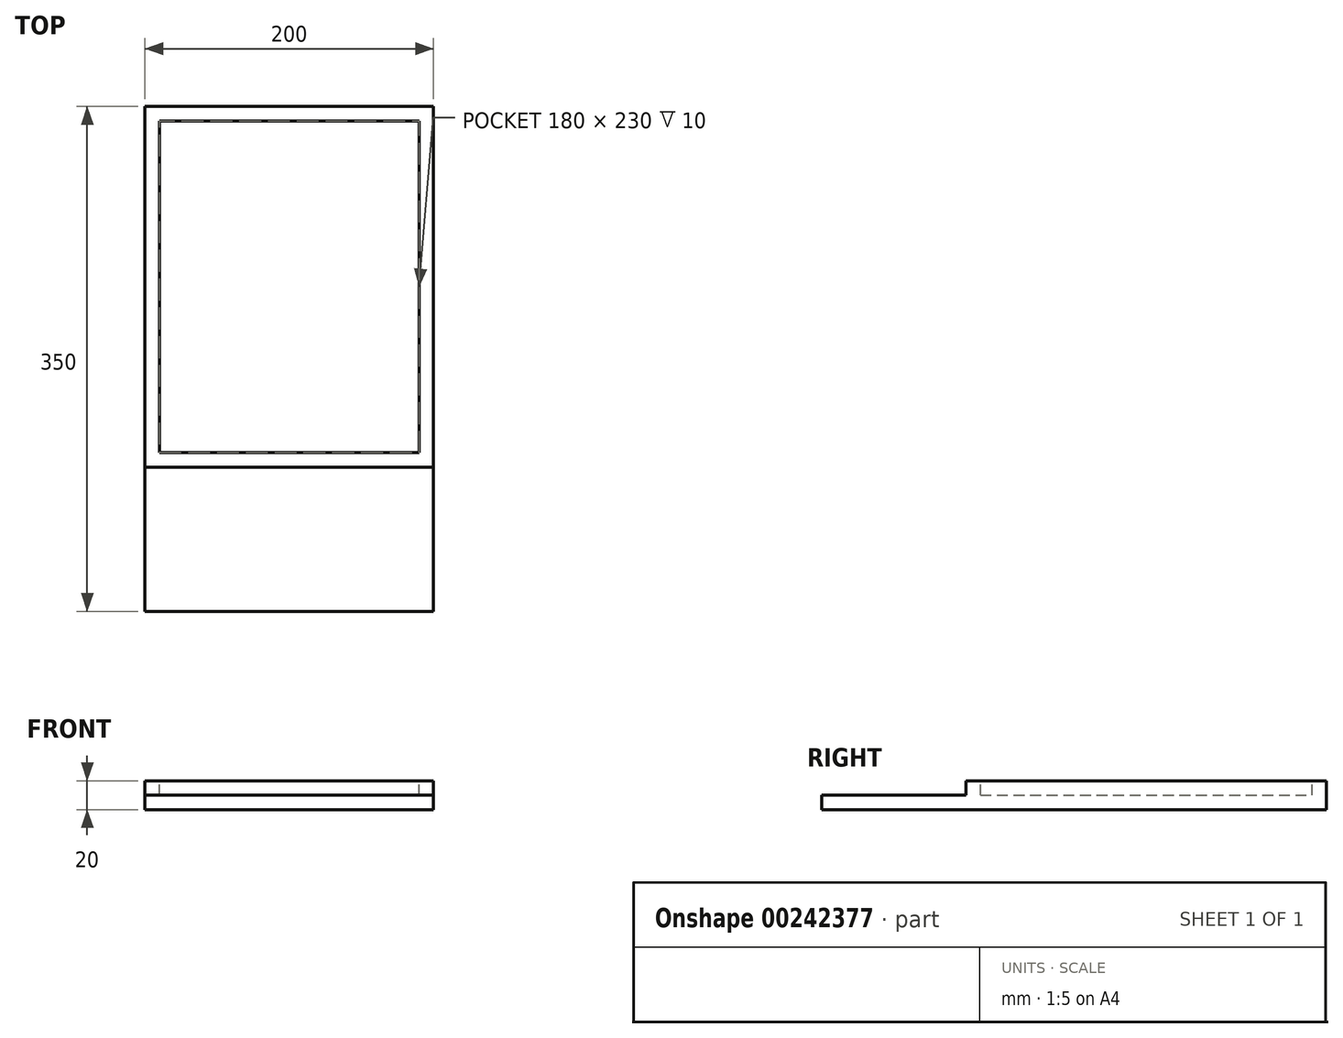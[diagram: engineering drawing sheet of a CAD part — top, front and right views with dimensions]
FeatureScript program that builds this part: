
annotation { "Feature Type Name" : "Feature", "Feature Type Description" : "" }
export const myFeature = defineFeature(function(context is Context, id is Id, definition is map)
    precondition{}
    {
        {
            var Q0;
            Q0=qCreatedBy(makeId("Top.planeOp"),FACE);
            var sketch = newSketch(context, id + "F0", { "sketchPlane" : qUnion([Q0])});
            skLineSegment(sketch, "E0.bottom", {"start": v(-59, -123.05) * mm, "end": v(141, -123.05) * mm});
            skLineSegment(sketch, "E0.top", {"start": v(-59, 126.95) * mm, "end": v(141, 126.95) * mm});
            skLineSegment(sketch, "E0.left", {"start": v(-59, -123.05) * mm, "end": v(-59, 126.95) * mm});
            skLineSegment(sketch, "E0.right", {"start": v(141, -123.05) * mm, "end": v(141, 126.95) * mm});
            skLineSegment(sketch, "E1.top", {"start": v(-59, -223.05) * mm, "end": v(141, -223.05) * mm});
            skLineSegment(sketch, "E1.left", {"start": v(-59, -123.05) * mm, "end": v(-59, -223.05) * mm});
            skLineSegment(sketch, "E1.right", {"start": v(141, -123.05) * mm, "end": v(141, -223.05) * mm});
            skSolve(sketch);
        }
        {
            var Q0;
            Q0=makeQuery(id+"F0.imprint","IMPRINT",FACE,{"disambiguationData":[TD([[makeQuery(id+"F0.imprint","IMPRINT",EDGE,{"derivedFrom":sQuery(id+"F0.wireOp",EDGE,"E0.top")}),-1.0]])]});
            extrude(context, id + "F1", {"entities" : qUnion([Q0]), "depth" : 200 * mm});
        }
        {
            var Q0;
            Q0=makeQuery(id+"F1.opExtrude","CAP_FACE",FACE,{"disambiguationData":[OSD([sQuery(id+"F0.wireOp",EDGE,"E0.top"),sQuery(id+"F0.wireOp",EDGE,"E0.left"),sQuery(id+"F0.wireOp",EDGE,"E0.right"),sQuery(id+"F0.wireOp",EDGE,"E0.bottom")])],"isStart":false});
            var sketch = newSketch(context, id + "F2", { "sketchPlane" : qUnion([Q0])});
            skLineSegment(sketch, "E2.0", {"start": v(-49, -113.05) * mm, "end": v(131, -113.05) * mm});
            skLineSegment(sketch, "E2.1", {"start": v(-49, -113.05) * mm, "end": v(-49, 116.95) * mm});
            skLineSegment(sketch, "E2.2", {"start": v(-49, 116.95) * mm, "end": v(131, 116.95) * mm});
            skLineSegment(sketch, "E2.3", {"start": v(131, -113.05) * mm, "end": v(131, 116.95) * mm});
            skSolve(sketch);
        }
        {
            var Q0;
            Q0=makeQuery(id+"F2.imprint","IMPRINT",FACE,{"disambiguationData":[TD([[makeQuery(id+"F2.imprint","IMPRINT",EDGE,{"derivedFrom":sQuery(id+"F2.wireOp",EDGE,"E2.0")}),1.0]])]});
            extrude(context, id + "F3", {"entities" : qUnion([Q0]), "operationType" : NewBodyOperationType.REMOVE, "oppositeDirection" : true, "depth" : 190 * mm});
        }
        {
            var Q0;
            Q0=makeQuery(id+"F1.opExtrude","CAP_FACE",FACE,{"disambiguationData":[OSD([sQuery(id+"F0.wireOp",EDGE,"E0.top"),sQuery(id+"F0.wireOp",EDGE,"E0.left"),sQuery(id+"F0.wireOp",EDGE,"E0.right"),sQuery(id+"F0.wireOp",EDGE,"E0.bottom")])],"isStart":false});
            extrude(context, id + "F4", {"entities" : qUnion([Q0]), "operationType" : NewBodyOperationType.REMOVE, "oppositeDirection" : true, "depth" : 180 * mm});
        }
        {
            var Q0;
            Q0=makeQuery(id+"F0.imprint","IMPRINT",FACE,{"disambiguationData":[TD([[makeQuery(id+"F0.imprint","IMPRINT",EDGE,{"derivedFrom":sQuery(id+"F0.wireOp",EDGE,"E0.bottom")}),-1.0]])]});
            extrude(context, id + "F5", {"entities" : qUnion([Q0]), "operationType" : NewBodyOperationType.ADD, "depth" : 10 * mm});
        }
    });
